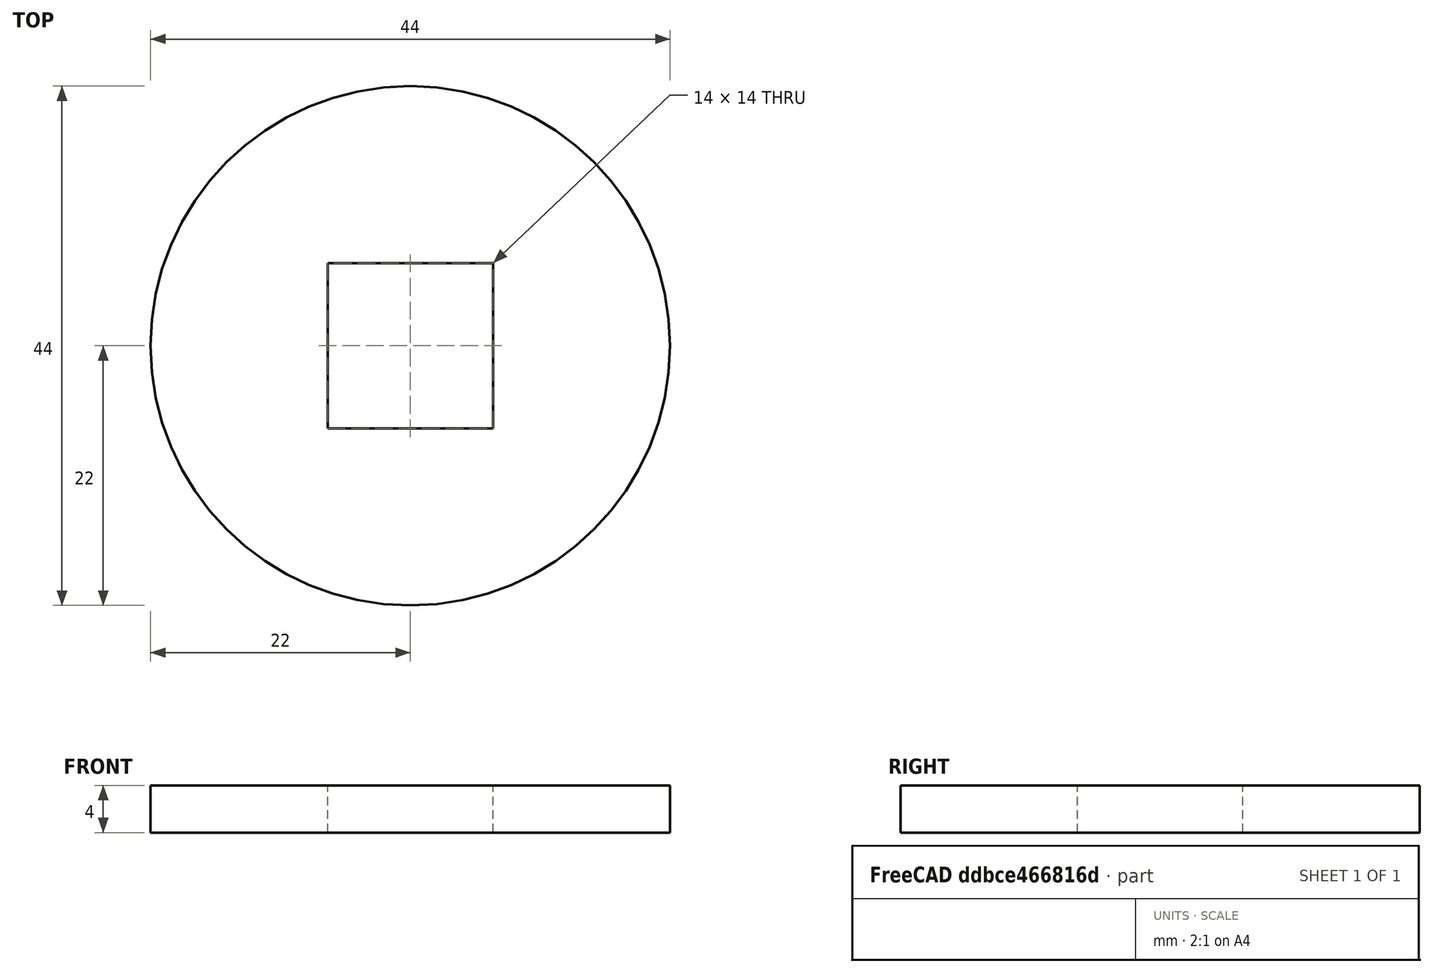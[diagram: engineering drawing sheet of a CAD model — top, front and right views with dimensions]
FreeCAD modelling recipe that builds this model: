
FCSTD DOCUMENT  (FreeCAD 0.15R4671 (Git))
Label: DIN440_CLASS_V_M14
License: CreativeCommons Attribution-ShareAlike
LicenseURL: http://creativecommons.org/licenses/by-sa/4.0/
objects: Sketcher::SketchObject×1, PartDesign::Pad×1
note: 3 computed .brp shape members not serialized (recipe doc carries the construction recipe); baked Part::Feature solids carry a one-line shape summary decoded from their .brp

FEATURE [Sketcher::SketchObject] Sketch
  sketch-geometry (5):
    g0: Circle CenterX=0 CenterY=0 CenterZ=0 NormalX=0 NormalY=0 NormalZ=1 Radius=22
    g1: LineSegment StartX=-7 StartY=7 StartZ=0 EndX=7 EndY=7 EndZ=0
    g2: LineSegment StartX=7 StartY=7 StartZ=0 EndX=7 EndY=-7 EndZ=0
    g3: LineSegment StartX=7 StartY=-7 StartZ=0 EndX=-7 EndY=-7 EndZ=0
    g4: LineSegment StartX=-7 StartY=-7 StartZ=0 EndX=-7 EndY=7 EndZ=0
  constraints (15):
    c: Coincident(g0,g-1)
    c: Radius(g0) = 22
    c: Coincident(g1,g2)
    c: Coincident(g2,g3)
    c: Coincident(g3,g4)
    c: Coincident(g4,g1)
    c: Horizontal(g1)
    c: Horizontal(g3)
    c: Vertical(g2)
    c: Vertical(g4)
    c: Equal(g1,g4)
    c: Equal(g4,g3)
    c: Equal(g3,g2)
    c: DistanceX(g1,g1) = 14
    c: Symmetric(g2,g1,g-1)
FEATURE [PartDesign::Pad] Pad
  Length = 4
  Length2 = 100
  Sketch = -> Sketch
  Type = 0
